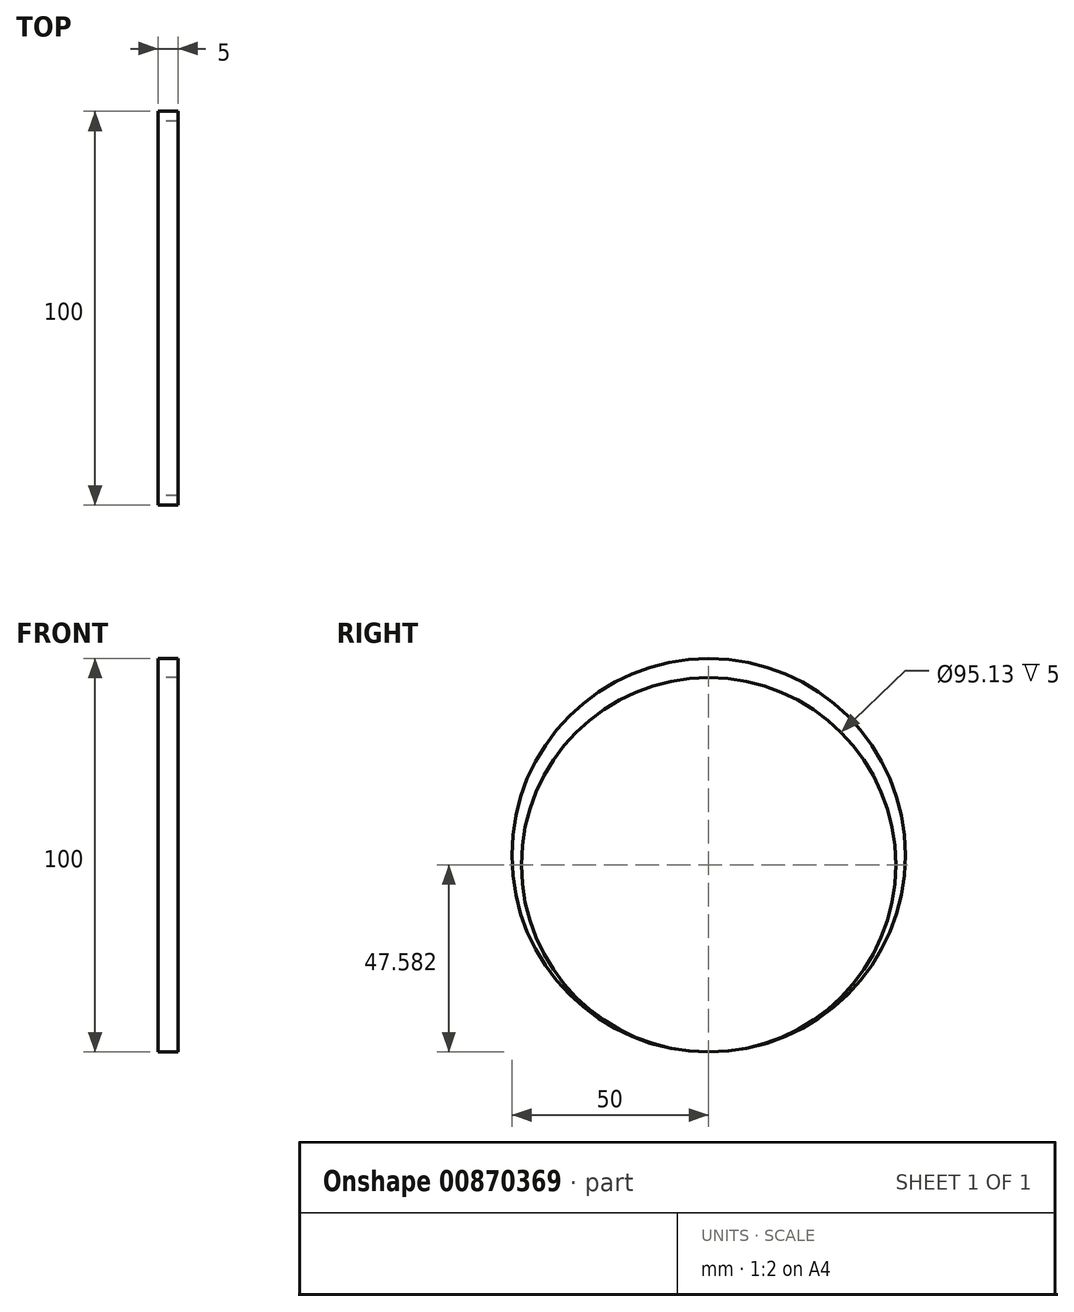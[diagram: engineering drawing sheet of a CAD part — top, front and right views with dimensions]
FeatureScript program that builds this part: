
annotation { "Feature Type Name" : "Feature", "Feature Type Description" : "" }
export const myFeature = defineFeature(function(context is Context, id is Id, definition is map)
    precondition{}
    {
        {
            var Q0;
            Q0=qCreatedBy(makeId("Right.planeOp"),FACE);
            var sketch = newSketch(context, id + "F0", { "sketchPlane" : qUnion([Q0])});
            skCircle(sketch, "E0", {"center": v(0, 0) * mm, "radius": 50 * mm});
            skCircle(sketch, "E1", {"center": v(0, -2.42) * mm, "radius": 47.57 * mm});
            skLineSegment(sketch, "E2", {"start": v(-16.78, 35.9) * mm, "end": v(0, 4.5) * mm});
            skLineSegment(sketch, "E3", {"start": v(0, 4.5) * mm, "end": v(-36.1, -33.38) * mm});
            skLineSegment(sketch, "E4", {"start": v(-1.58, 7.47) * mm, "end": v(-38.12, -30.87) * mm});
            skLineSegment(sketch, "E5", {"start": v(-4.1, 12.19) * mm, "end": v(-40.33, -27.63) * mm});
            skLineSegment(sketch, "E6", {"start": v(-42.05, -24.66) * mm, "end": v(-5.74, 15.25) * mm});
            skLineSegment(sketch, "E7", {"start": v(-7.56, 18.64) * mm, "end": v(-43.73, -21.13) * mm});
            skLineSegment(sketch, "E8", {"start": v(-45.23, -17.13) * mm, "end": v(-9.17, 21.66) * mm});
            skLineSegment(sketch, "E9", {"start": v(-10.8, 24.73) * mm, "end": v(-46.27, -13.43) * mm});
            skLineSegment(sketch, "E10", {"start": v(-46.92, -10.2) * mm, "end": v(-12.14, 27.22) * mm});
            skLineSegment(sketch, "E11", {"start": v(-13.86, 30.44) * mm, "end": v(-47.45, -5.7) * mm});
            skLineSegment(sketch, "E12", {"start": v(-47.57, -2.46) * mm, "end": v(-15, 32.57) * mm});
            skLineSegment(sketch, "E13", {"start": v(-17.34, 35.9) * mm, "end": v(-47.25, 3.07) * mm});
            skLineSegment(sketch, "E14", {"start": v(-46.27, 8.6) * mm, "end": v(-21.4, 35.9) * mm});
            skLineSegment(sketch, "E15", {"start": v(-24.98, 38.06) * mm, "end": v(24.98, 38.06) * mm});
            skLineSegment(sketch, "E16", {"start": v(28.19, 35.9) * mm, "end": v(-28.19, 35.9) * mm});
            skLineSegment(sketch, "E17", {"start": v(-32, 32.78) * mm, "end": v(32, 32.78) * mm});
            skLineSegment(sketch, "E18", {"start": v(34.4, 30.44) * mm, "end": v(-34.4, 30.44) * mm});
            skLineSegment(sketch, "E19", {"start": v(-37.14, 27.3) * mm, "end": v(37.14, 27.3) * mm});
            skLineSegment(sketch, "E20", {"start": v(39.06, 24.73) * mm, "end": v(-39.06, 24.73) * mm});
            skLineSegment(sketch, "E21", {"start": v(-41.02, 21.66) * mm, "end": v(41.02, 21.66) * mm});
            skLineSegment(sketch, "E22", {"start": v(42.65, 18.64) * mm, "end": v(-42.65, 18.64) * mm});
            skLineSegment(sketch, "E23", {"start": v(-44.16, 15.25) * mm, "end": v(44.16, 15.25) * mm});
            skLineSegment(sketch, "E24", {"start": v(45.27, 12.19) * mm, "end": v(-45.27, 12.19) * mm});
            skLineSegment(sketch, "E25", {"start": v(-46.53, 7.47) * mm, "end": v(46.53, 7.47) * mm});
            skLineSegment(sketch, "E26", {"start": v(47.06, 4.5) * mm, "end": v(-47.06, 4.5) * mm});
            skLineSegment(sketch, "E27.MirrorCS", {"start": v(16.78, 35.9) * mm, "end": v(0, 4.5) * mm});
            skLineSegment(sketch, "E28.MirrorCS", {"start": v(0, 4.5) * mm, "end": v(36.1, -33.38) * mm});
            skLineSegment(sketch, "E29.MirrorCS", {"start": v(1.58, 7.47) * mm, "end": v(38.12, -30.87) * mm});
            skLineSegment(sketch, "E30.MirrorCS", {"start": v(4.1, 12.19) * mm, "end": v(40.33, -27.63) * mm});
            skLineSegment(sketch, "E31.MirrorCS", {"start": v(42.05, -24.66) * mm, "end": v(5.74, 15.25) * mm});
            skLineSegment(sketch, "E32.MirrorCS", {"start": v(7.56, 18.64) * mm, "end": v(43.73, -21.13) * mm});
            skLineSegment(sketch, "E33.MirrorCS", {"start": v(45.23, -17.13) * mm, "end": v(9.17, 21.66) * mm});
            skLineSegment(sketch, "E34.MirrorCS", {"start": v(10.8, 24.73) * mm, "end": v(46.27, -13.43) * mm});
            skLineSegment(sketch, "E35.MirrorCS", {"start": v(46.92, -10.2) * mm, "end": v(12.14, 27.22) * mm});
            skLineSegment(sketch, "E36.MirrorCS", {"start": v(13.86, 30.44) * mm, "end": v(47.45, -5.7) * mm});
            skLineSegment(sketch, "E37.MirrorCS", {"start": v(47.57, -2.46) * mm, "end": v(15, 32.57) * mm});
            skLineSegment(sketch, "E38.MirrorCS", {"start": v(17.34, 35.9) * mm, "end": v(47.25, 3.07) * mm});
            skLineSegment(sketch, "E39.MirrorCS", {"start": v(46.27, 8.6) * mm, "end": v(21.4, 35.9) * mm});
            skSolve(sketch);
        }
        {
            var Q0;
            Q0 = qSketchRegion(id + "F0", true);
            extrude(context, id + "F1", {"entities" : qUnion([Q0]), "depth" : 5 * mm, "offsetDistance" : 25 * mm});
        }
    });
